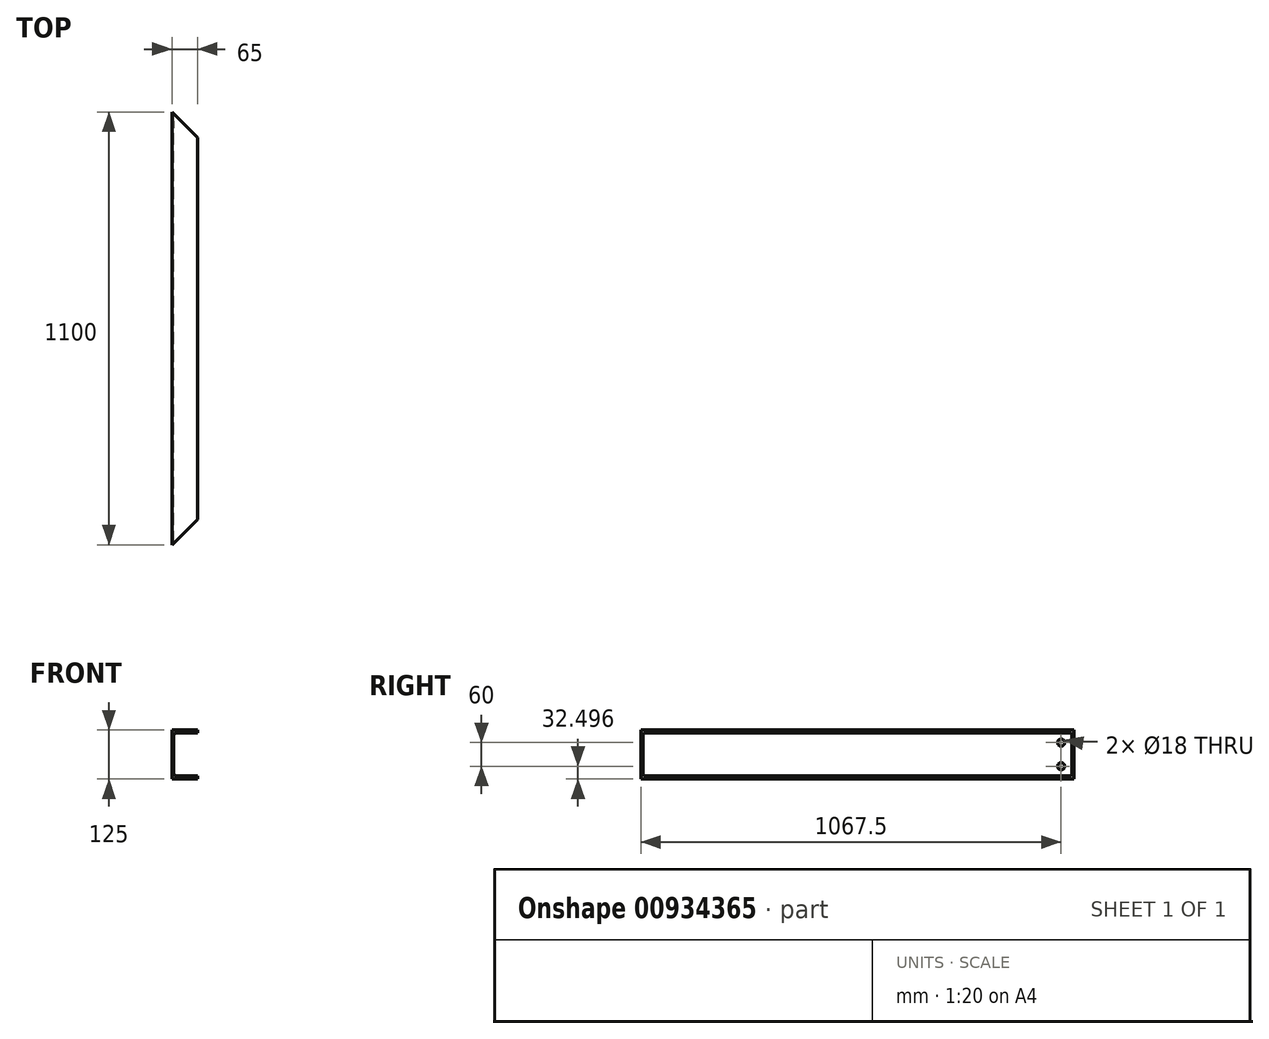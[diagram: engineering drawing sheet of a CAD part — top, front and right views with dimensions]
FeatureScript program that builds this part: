
annotation { "Feature Type Name" : "Feature", "Feature Type Description" : "" }
export const myFeature = defineFeature(function(context is Context, id is Id, definition is map)
    precondition{}
    {
        {
            var Q0;
            Q0=qCreatedBy(makeId("Front.planeOp"),FACE);
            var sketch = newSketch(context, id + "F0", { "sketchPlane" : qUnion([Q0])});
            skLineSegment(sketch, "E0", {"start": v(-25.08, -61.45) * mm, "end": v(-25.08, 63.55) * mm});
            skLineSegment(sketch, "E1", {"start": v(-25.08, 63.55) * mm, "end": v(39.92, 63.55) * mm});
            skLineSegment(sketch, "E2", {"start": v(39.92, 63.55) * mm, "end": v(39.92, 56.05) * mm});
            skLineSegment(sketch, "E3", {"start": v(39.92, 56.05) * mm, "end": v(-12.38, 56.05) * mm});
            skLineSegment(sketch, "E4", {"start": v(-25.08, -61.45) * mm, "end": v(39.92, -61.45) * mm});
            skLineSegment(sketch, "E5", {"start": v(39.92, -61.45) * mm, "end": v(39.92, -53.95) * mm});
            skLineSegment(sketch, "E6", {"start": v(39.92, -53.95) * mm, "end": v(-12.38, -53.95) * mm});
            skLineSegment(sketch, "E7", {"start": v(-20.38, -45.95) * mm, "end": v(-20.38, 48.05) * mm});
            skPoint(sketch, "E8.visualSharp", {"position": v(-20.38, 56.05) * mm});
            skArc(sketch, "E8.filletArc", {"start": v(-12.38, 56.05) * mm, "mid": v(-18.03, 53.7) * mm, "end": v(-20.38, 48.05) * mm});
            skPoint(sketch, "E9.visualSharp", {"position": v(-20.38, -53.95) * mm});
            skArc(sketch, "E9.filletArc", {"start": v(-20.38, -45.95) * mm, "mid": v(-18.03, -51.61) * mm, "end": v(-12.38, -53.95) * mm});
            skSolve(sketch);
        }
        {
            var Q0;
            Q0=makeQuery(id+"F0.imprint","IMPRINT",FACE,{"disambiguationData":[TD([[makeQuery(id+"F0.imprint","IMPRINT",EDGE,{"derivedFrom":sQuery(id+"F0.wireOp",EDGE,"E0")}),-1.0]])]});
            extrude(context, id + "F1", {"entities" : qUnion([Q0]), "depth" : 1100 * mm, "offsetDistance" : 25 * mm});
        }
        {
            var Q0;
            Q0=makeQuery(id+"F1.opExtrude","SWEPT_FACE",FACE,{"disambiguationData":[OSD([sQuery(id+"F0.wireOp",EDGE,"E1")])]});
            var sketch = newSketch(context, id + "F2", { "sketchPlane" : qUnion([Q0])});
            skLineSegment(sketch, "E10", {"start": v(39.92, -1100) * mm, "end": v(39.92, -1035) * mm});
            skLineSegment(sketch, "E11", {"start": v(39.92, -1035) * mm, "end": v(-25.08, -1100) * mm});
            skLineSegment(sketch, "E12", {"start": v(39.92, 0) * mm, "end": v(39.92, -65) * mm});
            skLineSegment(sketch, "E13", {"start": v(39.92, -65) * mm, "end": v(-25.08, 0) * mm});
            skSolve(sketch);
        }
        {
            var Q0;
            Q0=makeQuery(id+"F2.imprint","IMPRINT",FACE,{"disambiguationData":[TD([[makeQuery(id+"F2.imprint","IMPRINT",EDGE,{"derivedFrom":sQuery(id+"F2.wireOp",EDGE,"E12")}),1.0]])]});
            var Q1;
            Q1=makeQuery(id+"F2.imprint","IMPRINT",FACE,{"disambiguationData":[TD([[makeQuery(id+"F2.imprint","IMPRINT",EDGE,{"derivedFrom":sQuery(id+"F2.wireOp",EDGE,"E10")}),1.0]])]});
            extrude(context, id + "F3", {"entities" : qUnion([Q0, Q1]), "operationType" : NewBodyOperationType.REMOVE, "endBound" : BoundingType.THROUGH_ALL, "oppositeDirection" : true, "depth" : 25 * mm, "offsetDistance" : 25 * mm});
        }
        {
            var Q0;
            Q0=makeQuery(id+"F1.opExtrude","SWEPT_FACE",FACE,{"disambiguationData":[OSD([sQuery(id+"F0.wireOp",EDGE,"E0")])]});
            var sketch = newSketch(context, id + "F4", { "sketchPlane" : qUnion([Q0])});
            skPoint(sketch, "E14.endSnap0", {"position": v(0, 1.05) * mm});
            skLineSegment(sketch, "E15", {"start": v(32.5, 63.55) * mm, "end": v(32.5, 31.05) * mm, "construction": true});
            skLineSegment(sketch, "E16", {"start": v(32.5, 31.05) * mm, "end": v(32.5, -28.95) * mm, "construction": true});
            skCircle(sketch, "E17", {"center": v(32.5, 31.05) * mm, "radius": 9 * mm});
            skCircle(sketch, "E18", {"center": v(32.5, -28.95) * mm, "radius": 9 * mm});
            skSolve(sketch);
        }
        {
            var Q0;
            Q0 = qSketchRegion(id + "F4", true);
            extrude(context, id + "F5", {"entities" : qUnion([Q0]), "operationType" : NewBodyOperationType.REMOVE, "endBound" : BoundingType.THROUGH_ALL, "oppositeDirection" : true, "depth" : 25 * mm, "offsetDistance" : 25 * mm});
        }
    });
